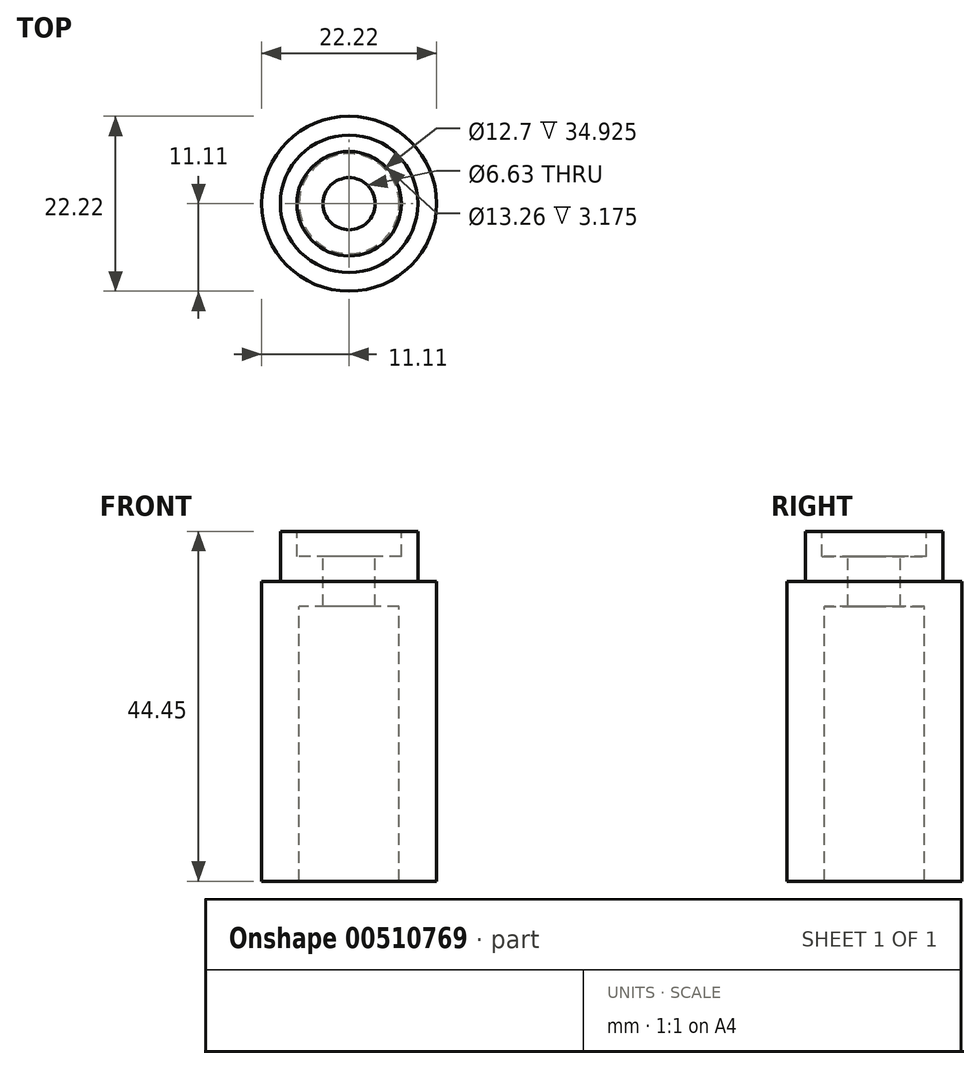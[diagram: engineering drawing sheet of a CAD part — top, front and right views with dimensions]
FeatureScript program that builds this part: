
annotation { "Feature Type Name" : "Feature", "Feature Type Description" : "" }
export const myFeature = defineFeature(function(context is Context, id is Id, definition is map)
    precondition{}
    {
        {
            var Q0;
            Q0=qCreatedBy(makeId("Front.planeOp"),FACE);
            var sketch = newSketch(context, id + "F0", { "sketchPlane" : qUnion([Q0])});
            skLineSegment(sketch, "E0", {"start": v(-8.73, 12.24) * mm, "end": v(-8.73, 5.9) * mm});
            skLineSegment(sketch, "E1", {"start": v(-8.73, 5.9) * mm, "end": v(-11.11, 5.9) * mm});
            skLineSegment(sketch, "E2", {"start": v(-11.11, 5.9) * mm, "end": v(-11.11, -32.2) * mm});
            skLineSegment(sketch, "E3", {"start": v(-11.11, -32.2) * mm, "end": v(-6.35, -32.2) * mm});
            skLineSegment(sketch, "E4", {"start": v(-6.63, 12.24) * mm, "end": v(-6.63, 9.07) * mm});
            skLineSegment(sketch, "E5", {"start": v(-6.63, 9.07) * mm, "end": v(-3.31, 9.07) * mm});
            skLineSegment(sketch, "E6", {"start": v(-8.73, 12.24) * mm, "end": v(-6.63, 12.24) * mm});
            skLineSegment(sketch, "E7", {"start": v(-3.31, 9.07) * mm, "end": v(-3.31, 2.72) * mm});
            skPoint(sketch, "E8.orphan", {"position": v(0, -32.2) * mm});
            skPoint(sketch, "E9.orphan", {"position": v(0, 9.07) * mm});
            skLineSegment(sketch, "E10", {"start": v(-6.35, -32.2) * mm, "end": v(-6.35, 2.72) * mm});
            skLineSegment(sketch, "E11", {"start": v(-6.35, 2.72) * mm, "end": v(-3.31, 2.72) * mm});
            skSolve(sketch);
        }
        {
            var Q0;
            Q0=qCreatedBy(makeId("Front.planeOp"),FACE);
            var sketch = newSketch(context, id + "F1", { "sketchPlane" : qUnion([Q0])});
            skLineSegment(sketch, "E12", {"start": v(0, 0) * mm, "end": v(0, -99.9) * mm});
            skSolve(sketch);
        }
        {
            var Q0;
            Q0 = qSketchRegion(id + "F0", true);
            var Q1;
            Q1=sQuery(id+"F1.wireOp",EDGE,"E12");
            revolve(context, id + "F2", {"entities" : qUnion([Q0]), "axis" : qUnion([Q1]), "revolveType" : RevolveType.FULL});
        }
    });
